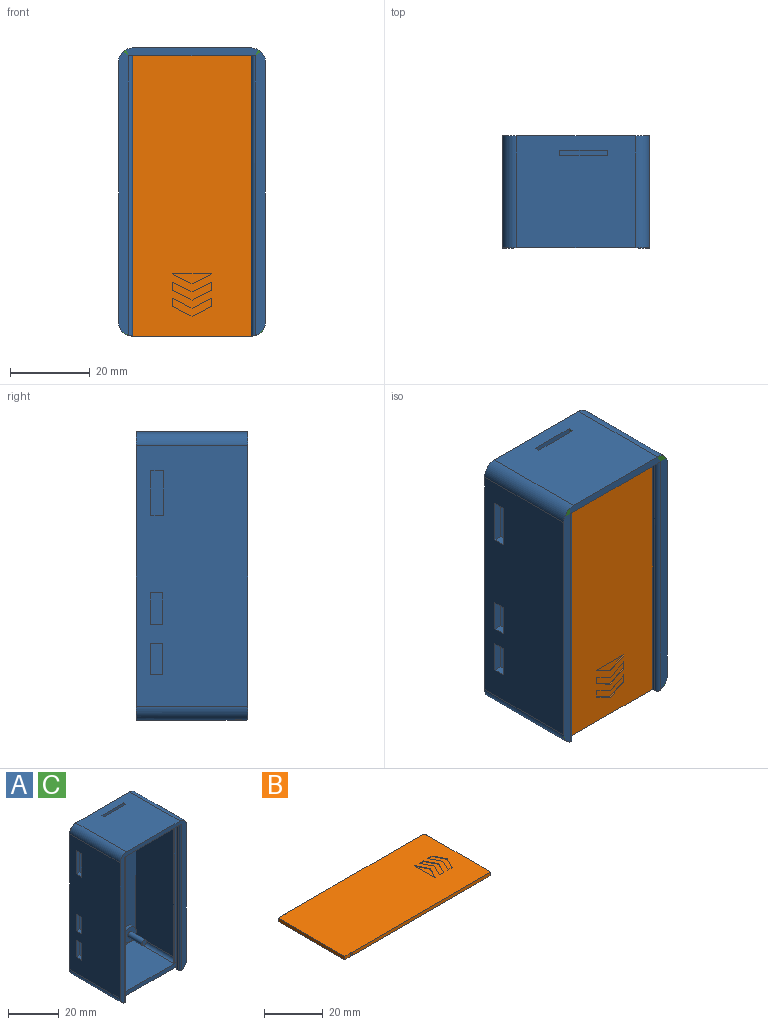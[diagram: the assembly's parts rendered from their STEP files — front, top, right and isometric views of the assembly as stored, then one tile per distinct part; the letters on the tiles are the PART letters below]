
ASSEMBLY  parts=3 mates=1
PART A: 70 faces, bbox 36.8x28x72.2 mm
  f0: plane 70.21x1.2mm, normal (0,1,0), area 83.9mm2, adj f3,f7,f8,f10,f26,f27
  f1: plane 72.06x36.8mm, normal (0,-1,0), area 414.2mm2, adj f2,f3,f4,f45,f46,f47,f49,f50
  f2: cylinder r=3.5mm len=28mm, axis (0,1,0), area 151.6mm2, adj f1,f6,f9,f23,f24,f47,f48,f67
  f3: cylinder r=3.5mm len=28mm, axis (0,1,0), area 151.6mm2, adj f0,f1,f7,f10,f24,f45,f48,f67
  f4: plane 31.81x26.01mm, normal (0,0,-1), area 760mm2, adj f1,f9,f10,f11,f14,f17,f18,f20
  f5: plane 65.2x22.5mm, normal (1,0,0), area 1382.4mm2, adj f11,f12,f17,f21,f29,f30,f31,f32
  f6: plane 66.64x1.5mm, normal (-1,0,0), area 100mm2, adj f2,f23,f24,f28
  f7: plane 66.64x1.5mm, normal (1,0,0), area 100mm2, adj f0,f3,f24,f27
  f8: plane 2.82x1.5mm, normal (1,0,0), area 4.2mm2, adj f0,f24,f26,f27
  f9: plane 70.2x0.7mm, normal (-1,0,0), area 49.2mm2, adj f2,f4,f23,f69
  f10: plane 70.2x0.7mm, normal (1,0,0), area 49.2mm2, adj f0,f3,f4,f68
  f11: cylinder r=1.5mm len=22.5mm, axis (0,1,0), area 53mm2, adj f4,f5,f17,f21
  f12: cylinder r=1.5mm len=22.5mm, axis (0,1,0), area 53mm2, adj f5,f16,f17,f21
  f13: plane 65.2x22.5mm, normal (-1,0,0), area 1467mm2, adj f14,f15,f17,f19
  f14: cylinder r=1.5mm len=22.5mm, axis (0,1,0), area 53mm2, adj f4,f13,f17,f19
  f15: cylinder r=1.5mm len=22.5mm, axis (0,1,0), area 53mm2, adj f13,f16,f17,f19
  f16: plane 29.8x22.8mm, normal (0,0,1), area 679.4mm2, adj f12,f15,f17,f18,f20,f24
  f17: plane 68.2x32.8mm, normal (0,-1,0), area 2090.1mm2, adj f4,f5,f11,f12,f13,f14,f15,f16
  f18: plane 68.2x0.3mm, normal (-1,0,0), area 20.4mm2, adj f4,f16,f19,f24
  f19: plane 68.2x1.5mm, normal (0,1,0), area 101.3mm2, adj f13,f14,f15,f18
  f20: plane 68.2x0.3mm, normal (1,0,0), area 20.4mm2, adj f4,f16,f21,f24
  f21: plane 68.2x1.5mm, normal (0,1,0), area 101.3mm2, adj f5,f11,f12,f20
  f22: plane 2.82x1.5mm, normal (-1,0,0), area 4.2mm2, adj f23,f24,f25,f28
  f23: plane 70.21x1.2mm, normal (0,1,0), area 83.9mm2, adj f2,f6,f9,f22,f25,f28
  f24: plane 70.21x32.2mm, normal (0,-1,0), area 227.3mm2, adj f2,f3,f6,f7,f8,f16,f18,f20
  f25: plane 1.51x1.21mm, normal (0,0,-1), area 1.8mm2, adj f4,f22,f23,f24
  f26: plane 1.51x1.21mm, normal (0,0,-1), area 1.8mm2, adj f0,f4,f8,f24
  f27: cylinder r=0.27mm len=1.5mm, axis (0,1,0), area 1.3mm2, adj f0,f7,f8,f24
  f28: cylinder r=0.27mm len=1.5mm, axis (0,1,0), area 1.3mm2, adj f6,f22,f23,f24
  f29: plane 8x2mm, normal (0,-1,0), area 16mm2, adj f5,f30,f32,f45
  f30: plane 3.05x2mm, normal (0,0,1), area 6.1mm2, adj f5,f29,f31,f45
  f31: plane 8x2mm, normal (0,1,0), area 16mm2, adj f5,f30,f32,f45
  f32: plane 3.05x2mm, normal (0,0,-1), area 6.1mm2, adj f5,f29,f31,f45
  f33: plane 3.2x2mm, normal (0,0,-1), area 6.4mm2, adj f5,f34,f36,f45
  f34: plane 11.2x2mm, normal (0,-1,0), area 22.4mm2, adj f5,f33,f35,f45
  f35: plane 3.2x2mm, normal (0,0,1), area 6.4mm2, adj f5,f34,f36,f45
  f36: plane 11.2x2mm, normal (0,1,0), area 22.4mm2, adj f5,f33,f35,f45
  f37: plane 8x2mm, normal (0,1,0), area 16mm2, adj f5,f38,f40,f45
  f38: plane 3.05x2mm, normal (0,0,-1), area 6.1mm2, adj f5,f37,f39,f45
  f39: plane 8x2mm, normal (0,-1,0), area 16mm2, adj f5,f38,f40,f45
  f40: plane 3.05x2mm, normal (0,0,1), area 6.1mm2, adj f5,f37,f39,f45
  f41: plane 2x1.27mm, normal (-1,0,0), area 2.5mm2, adj f4,f42,f44,f46
  f42: plane 12.01x2mm, normal (0,-1,0), area 24mm2, adj f4,f41,f43,f46
  f43: plane 2x1.27mm, normal (1,0,0), area 2.5mm2, adj f4,f42,f44,f46
  f44: plane 12.01x2mm, normal (0,1,0), area 24mm2, adj f4,f41,f43,f46
  f45: plane 65.2x28mm, normal (-1,0,0), area 1741mm2, adj f1,f3,f29,f30,f31,f32,f33,f34
  f46: plane 29.8x28mm, normal (0,0,1), area 819.2mm2, adj f1,f41,f42,f43,f44,f49,f50,f67
  f47: plane 65.2x28mm, normal (1,0,0), area 1825.7mm2, adj f1,f2,f50,f67
  f48: plane 29.8x24.8mm, normal (0,0,-1), area 739.1mm2, adj f2,f3,f24,f67
  f49: cylinder r=3.5mm len=28mm, axis (0,1,0), area 153.9mm2, adj f1,f45,f46,f67
  f50: cylinder r=3.5mm len=28mm, axis (0,1,0), area 153.9mm2, adj f1,f46,f47,f67
  f51: cylinder r=3.4mm len=6.8mm, axis (0,1,0), area 34.2mm2, adj f17,f54
  f52: plane 2.6x2.6mm, normal (0,-1,0), area 5.3mm2, adj f53
  f53: cylinder r=1.3mm len=7.9mm, axis (0,1,0), area 64.5mm2, adj f52,f54
  f54: plane 6.8x6.8mm, normal (0,-1,0), area 31mm2, adj f51,f53
  f55: cylinder r=3.4mm len=6.8mm, axis (0,1,0), area 34.2mm2, adj f17,f56
  f56: plane 6.8x6.8mm, normal (0,-1,0), area 31mm2, adj f55,f58
  f57: plane 2.6x2.6mm, normal (0,-1,0), area 5.3mm2, adj f58
  f58: cylinder r=1.3mm len=7.9mm, axis (0,-1,0), area 64.5mm2, adj f56,f57
  f59: cylinder r=3.4mm len=6.8mm, axis (0,1,0), area 34.2mm2, adj f17,f60
  f60: plane 6.8x6.8mm, normal (0,-1,0), area 31mm2, adj f59,f62
  f61: plane 2.6x2.6mm, normal (0,-1,0), area 5.3mm2, adj f62
  f62: cylinder r=1.3mm len=7.9mm, axis (0,1,0), area 64.5mm2, adj f60,f61
  f63: cylinder r=3.4mm len=6.8mm, axis (0,1,0), area 34.2mm2, adj f17,f64
  f64: plane 6.8x6.8mm, normal (0,-1,0), area 31mm2, adj f63,f66
  f65: plane 2.6x2.6mm, normal (0,-1,0), area 5.3mm2, adj f66
  f66: cylinder r=1.3mm len=7.9mm, axis (0,-1,0), area 64.5mm2, adj f64,f65
  f67: plane 72.2x36.8mm, normal (0,1,0), area 2646.7mm2, adj f2,f3,f45,f46,f47,f48,f49,f50
  f68: cylinder r=1mm len=70.2mm, axis (0,0,-1), area 110.2mm2, adj f1,f3,f4,f10
  f69: cylinder r=1mm len=70.2mm, axis (0,0,-1), area 110.2mm2, adj f1,f2,f4,f9
PART B: 32 faces, bbox 70.2x32x1.4 mm
  f0: plane 70.21x32mm, normal (0,0,1), area 2194.3mm2, adj f1,f2,f4,f5,f6,f7,f8,f9
  f1: plane 66.22x1.4mm, normal (0,1,0), area 92.7mm2, adj f0,f3,f9,f10
  f2: plane 66.22x1.4mm, normal (0,-1,0), area 92.7mm2, adj f0,f3,f8,f11
  f3: plane 70.21x32mm, normal (0,0,-1), area 2246.1mm2, adj f1,f2,f4,f5,f6,f7,f8,f9
  f4: plane 29.62x1.4mm, normal (1,0,0), area 41.5mm2, adj f0,f3,f10,f11
  f5: plane 2.82x1.4mm, normal (0,1,0), area 3.9mm2, adj f0,f3,f7,f9
  f6: plane 2.82x1.4mm, normal (0,-1,0), area 3.9mm2, adj f0,f3,f7,f8
  f7: plane 32x1.4mm, normal (-1,0,0), area 44.8mm2, adj f0,f3,f5,f6
  f8: cylinder r=0.38mm len=1.4mm, axis (0,0,-1), area 1.7mm2, adj f0,f2,f3,f6
  f9: cylinder r=0.38mm len=1.4mm, axis (0,0,-1), area 1.7mm2, adj f0,f1,f3,f5
  f10: cylinder r=1.96mm len=1.4mm, axis (0,0,1), area 1.8mm2, adj f0,f1,f3,f4
  f11: cylinder r=1.96mm len=1.4mm, axis (0,0,1), area 1.8mm2, adj f0,f2,f3,f4
  f12: plane 4.81x2.47mm, normal (0.89,0.46,0), area 1.4mm2, adj f0,f13,f17,f18
  f13: plane 4.81x2.47mm, normal (0.89,-0.46,0), area 1.4mm2, adj f0,f12,f14,f18
  f14: plane 2.03x0.25mm, normal (0,1,0), area 0.5mm2, adj f0,f13,f15,f18
  f15: plane 4.81x2.47mm, normal (-0.89,0.46,0), area 1.4mm2, adj f0,f14,f16,f18
  f16: plane 4.81x2.47mm, normal (-0.89,-0.46,0), area 1.4mm2, adj f0,f15,f17,f18
  f17: plane 2.03x0.25mm, normal (0,-1,0), area 0.5mm2, adj f0,f12,f16,f18
  f18: plane 9.63x4.5mm, normal (0,0,1), area 19.6mm2, adj f12,f13,f14,f15,f16,f17
  f19: plane 4.81x2.47mm, normal (-0.89,0.46,0), area 1.4mm2, adj f0,f20,f23,f24
  f20: plane 4.81x2.47mm, normal (-0.89,-0.46,0), area 1.4mm2, adj f0,f19,f21,f24
  f21: plane 0.25x0.09mm, normal (0,-1,0), area 0mm2, adj f0,f20,f22,f24
  f22: plane 9.63x0.25mm, normal (1,0,0), area 2.4mm2, adj f0,f21,f23,f24
  f23: plane 0.25x0.09mm, normal (0,1,0), area 0mm2, adj f0,f19,f22,f24
  f24: plane 9.63x2.56mm, normal (0,0,1), area 12.8mm2, adj f19,f20,f21,f22,f23
  f25: plane 4.81x2.47mm, normal (0.89,0.46,0), area 1.4mm2, adj f0,f26,f30,f31
  f26: plane 4.81x2.47mm, normal (0.89,-0.46,0), area 1.4mm2, adj f0,f25,f27,f31
  f27: plane 2.03x0.25mm, normal (0,1,0), area 0.5mm2, adj f0,f26,f28,f31
  f28: plane 4.81x2.47mm, normal (-0.89,0.46,0), area 1.4mm2, adj f0,f27,f29,f31
  f29: plane 4.81x2.47mm, normal (-0.89,-0.46,0), area 1.4mm2, adj f0,f28,f30,f31
  f30: plane 2.03x0.25mm, normal (0,-1,0), area 0.5mm2, adj f0,f25,f29,f31
  f31: plane 9.63x4.5mm, normal (0,0,1), area 19.6mm2, adj f25,f26,f27,f28,f29,f30
PART C: same geometry as A
PLACE A t=(19.37,-26.85,9.03)mm
PLACE B rot(axis=(0.58,0.58,-0.58),120deg) t=(19.37,-50.15,8.03)mm
PLACE C t=(19.37,-26.85,9.03)mm
MATE fastened B.f3 <-> A.f24  axis (0,1,0) through (19.37,-50.15,-27.07)mm
